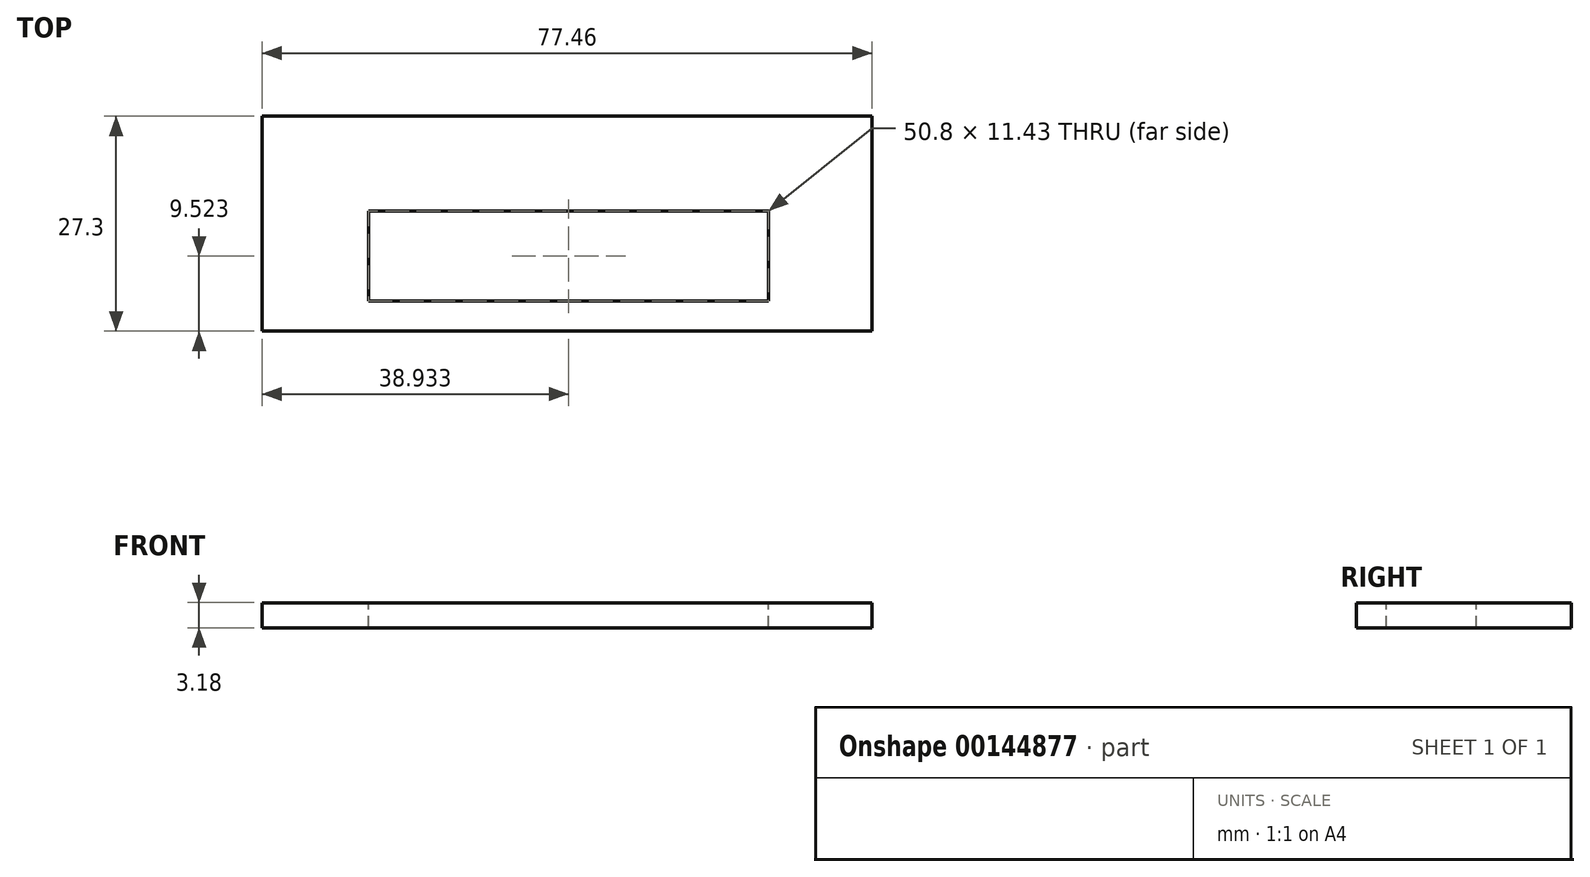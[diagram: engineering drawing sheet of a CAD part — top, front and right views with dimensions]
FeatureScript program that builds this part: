
annotation { "Feature Type Name" : "Feature", "Feature Type Description" : "" }
export const myFeature = defineFeature(function(context is Context, id is Id, definition is map)
    precondition{}
    {
        {
            var Q0;
            Q0=qCreatedBy(makeId("Top.planeOp"),FACE);
            var sketch = newSketch(context, id + "F0", { "sketchPlane" : qUnion([Q0])});
            skLineSegment(sketch, "E0.bottom", {"start": v(-38.73, 13.65) * mm, "end": v(38.73, 13.65) * mm});
            skLineSegment(sketch, "E0.top", {"start": v(-38.73, -13.65) * mm, "end": v(38.73, -13.65) * mm});
            skLineSegment(sketch, "E0.left", {"start": v(-38.73, 13.65) * mm, "end": v(-38.73, -13.65) * mm});
            skLineSegment(sketch, "E0.right", {"start": v(38.73, 13.65) * mm, "end": v(38.73, -13.65) * mm});
            skPoint(sketch, "E0.middle", {"position": v(0, 0) * mm});
            skPoint(sketch, "E1", {"position": v(33.83, 13.65) * mm});
            skPoint(sketch, "E2", {"position": v(-33.83, 13.65) * mm});
            skLineSegment(sketch, "E3.bottom", {"start": v(-33.83, 13.65) * mm, "end": v(-25.2, 13.65) * mm});
            skLineSegment(sketch, "E3.top", {"start": v(-33.83, 16.83) * mm, "end": v(-25.2, 16.83) * mm});
            skLineSegment(sketch, "E3.left", {"start": v(-33.83, 13.65) * mm, "end": v(-33.83, 16.83) * mm});
            skLineSegment(sketch, "E3.right", {"start": v(-25.2, 13.65) * mm, "end": v(-25.2, 16.83) * mm});
            skLineSegment(sketch, "E4.bottom", {"start": v(33.83, 13.65) * mm, "end": v(25.2, 13.65) * mm});
            skLineSegment(sketch, "E4.top", {"start": v(33.83, 16.83) * mm, "end": v(25.2, 16.83) * mm});
            skLineSegment(sketch, "E4.left", {"start": v(33.83, 13.65) * mm, "end": v(33.83, 16.83) * mm});
            skLineSegment(sketch, "E4.right", {"start": v(25.2, 13.65) * mm, "end": v(25.2, 16.83) * mm});
            skLineSegment(sketch, "E5.bottom", {"start": v(-33.83, -13.65) * mm, "end": v(-25.2, -13.65) * mm});
            skLineSegment(sketch, "E5.top", {"start": v(-33.83, -16.83) * mm, "end": v(-25.2, -16.83) * mm});
            skLineSegment(sketch, "E5.left", {"start": v(-33.83, -13.65) * mm, "end": v(-33.83, -16.83) * mm});
            skLineSegment(sketch, "E5.right", {"start": v(-25.2, -13.65) * mm, "end": v(-25.2, -16.83) * mm});
            skLineSegment(sketch, "E6.bottom", {"start": v(25.2, -13.65) * mm, "end": v(33.83, -13.65) * mm});
            skLineSegment(sketch, "E6.top", {"start": v(25.2, -16.83) * mm, "end": v(33.83, -16.83) * mm});
            skLineSegment(sketch, "E6.left", {"start": v(25.2, -13.65) * mm, "end": v(25.2, -16.83) * mm});
            skLineSegment(sketch, "E6.right", {"start": v(33.83, -13.65) * mm, "end": v(33.83, -16.83) * mm});
            skSolve(sketch);
        }
        {
            var Q0;
            Q0=makeQuery(id+"F0.imprint","IMPRINT",FACE,{"disambiguationData":[TD([[makeQuery(id+"F0.imprint","IMPRINT",EDGE,{"derivedFrom":sQuery(id+"F0.wireOp",EDGE,"E3.bottom")}),1.0]])]});
            var Q1;
            {var subQ1=sQuery(id+"F0.wireOp",EDGE,"E0.left");Q1=makeQuery(id+"F0.imprint","IMPRINT",FACE,{"disambiguationData":[TD([[makeQuery(id+"F0.imprint","IMPRINT",EDGE,{"derivedFrom":subQ1}),1.0]])]});}
            var Q2;
            Q2=makeQuery(id+"F0.imprint","IMPRINT",FACE,{"disambiguationData":[TD([[makeQuery(id+"F0.imprint","IMPRINT",EDGE,{"derivedFrom":sQuery(id+"F0.wireOp",EDGE,"E4.bottom")}),-1.0]])]});
            var Q3;
            Q3=makeQuery(id+"F0.imprint","IMPRINT",FACE,{"disambiguationData":[TD([[makeQuery(id+"F0.imprint","IMPRINT",EDGE,{"derivedFrom":sQuery(id+"F0.wireOp",EDGE,"E5.bottom")}),-1.0]])]});
            var Q4;
            Q4=makeQuery(id+"F0.imprint","IMPRINT",FACE,{"disambiguationData":[TD([[makeQuery(id+"F0.imprint","IMPRINT",EDGE,{"derivedFrom":sQuery(id+"F0.wireOp",EDGE,"E6.bottom")}),-1.0]])]});
            extrude(context, id + "F1", {"entities" : qUnion([Q0, Q1, Q2, Q3, Q4]), "depth" : 3.17 * mm});
        }
        {
            var Q0;
            Q0=makeQuery(id+"F1.opExtrude","CAP_FACE",FACE,{"disambiguationData":[OSD([sQuery(id+"F0.wireOp",EDGE,"E0.bottom"),sQuery(id+"F0.wireOp",EDGE,"E0.top"),sQuery(id+"F0.wireOp",EDGE,"E0.left"),sQuery(id+"F0.wireOp",EDGE,"E0.right"),sQuery(id+"F0.wireOp",EDGE,"E3.top"),sQuery(id+"F0.wireOp",EDGE,"E3.left"),sQuery(id+"F0.wireOp",EDGE,"E3.right"),sQuery(id+"F0.wireOp",EDGE,"E4.top"),sQuery(id+"F0.wireOp",EDGE,"E4.left"),sQuery(id+"F0.wireOp",EDGE,"E4.right"),sQuery(id+"F0.wireOp",EDGE,"E5.top"),sQuery(id+"F0.wireOp",EDGE,"E5.left"),sQuery(id+"F0.wireOp",EDGE,"E5.right"),sQuery(id+"F0.wireOp",EDGE,"E6.top"),sQuery(id+"F0.wireOp",EDGE,"E6.left"),sQuery(id+"F0.wireOp",EDGE,"E6.right")])],"isStart":false});
            var sketch = newSketch(context, id + "F2", { "sketchPlane" : qUnion([Q0])});
            skLineSegment(sketch, "E7.bottom", {"start": v(-25.2, 1.59) * mm, "end": v(25.6, 1.59) * mm});
            skLineSegment(sketch, "E7.top", {"start": v(-25.2, -9.84) * mm, "end": v(25.6, -9.84) * mm});
            skLineSegment(sketch, "E7.left", {"start": v(-25.2, 1.59) * mm, "end": v(-25.2, -9.84) * mm});
            skLineSegment(sketch, "E7.right", {"start": v(25.6, 1.59) * mm, "end": v(25.6, -9.84) * mm});
            skSolve(sketch);
        }
        {
            var Q0;
            Q0=makeQuery(id+"F2.imprint","IMPRINT",FACE,{"disambiguationData":[TD([[makeQuery(id+"F2.imprint","IMPRINT",EDGE,{"derivedFrom":sQuery(id+"F2.wireOp",EDGE,"E7.bottom")}),-1.0]])]});
            extrude(context, id + "F3", {"entities" : qUnion([Q0]), "operationType" : NewBodyOperationType.REMOVE, "oppositeDirection" : true, "depth" : 25.4 * mm});
        }
    });
